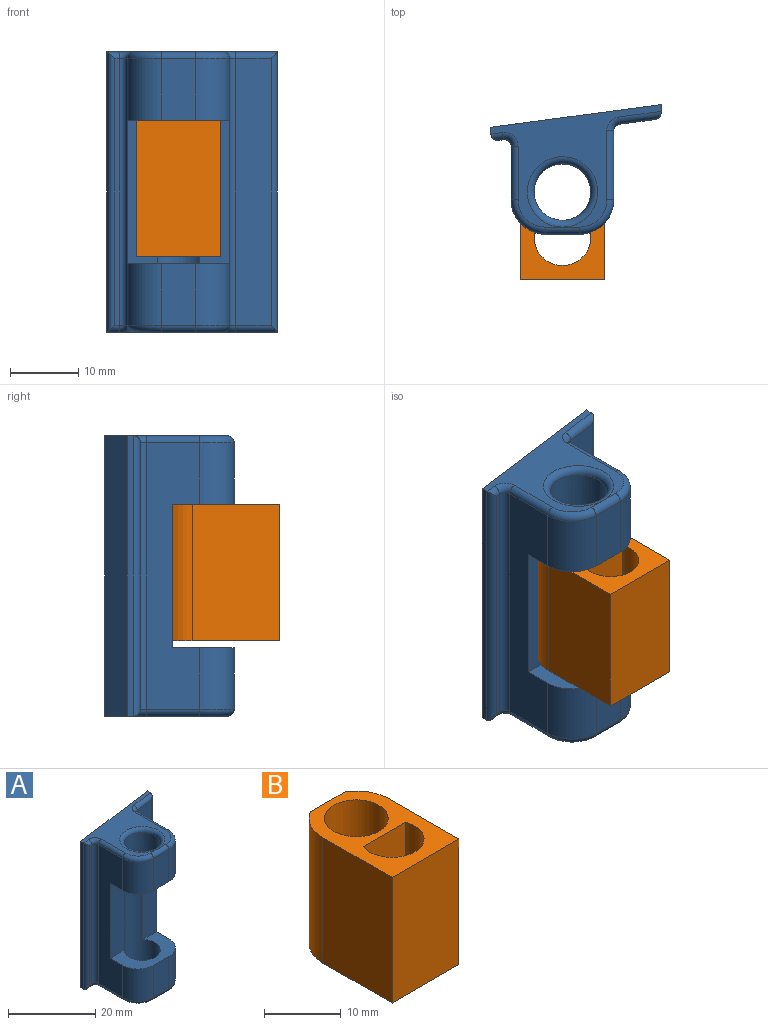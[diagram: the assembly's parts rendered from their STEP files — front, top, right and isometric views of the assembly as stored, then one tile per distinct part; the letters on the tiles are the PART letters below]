
ASSEMBLY  parts=2 mates=1
PART A: 44 faces, bbox 25x19.3x41 mm
  f0: plane 9x5mm, normal (0,-1,0), area 45mm2, adj f4,f5,f37,f42
  f1: plane 39x10.12mm, normal (1,0,0), area 310.9mm2, adj f4,f14,f19,f27,f33,f40,f42,f43
  f2: plane 39x7.86mm, normal (-1,0,0), area 222.5mm2, adj f5,f15,f22,f30,f34,f41,f42,f43
  f3: cylinder r=4.15mm len=39mm, axis (0,0,-1), area 611.2mm2, adj f38,f39,f40,f41,f42,f43
  f4: cylinder r=5mm len=9mm, axis (0,0,-1), area 70.7mm2, adj f0,f1,f35,f42
  f5: cylinder r=5mm len=9mm, axis (0,0,1), area 70.7mm2, adj f0,f2,f36,f42
  f6: plane 24.91x17.93mm, normal (0,0,-1), area 131.4mm2, adj f7,f9,f10,f25,f28,f29,f31,f32
  f7: plane 41x24.91mm, normal (-0.13,0.99,0), area 1030.4mm2, adj f6,f9,f10,f13
  f8: plane 39x5.2mm, normal (0.13,-0.99,0), area 204.7mm2, adj f20,f24,f27,f28
  f9: plane 41x1.12mm, normal (1,0,0), area 46.1mm2, adj f6,f7,f13,f20,f24,f28
  f10: plane 41x0.86mm, normal (-1,0,0), area 35.2mm2, adj f6,f7,f13,f25
  f11: plane 39x0.71mm, normal (0.13,-0.99,0), area 27.9mm2, adj f21,f25,f29,f30
  f12: plane 9x5mm, normal (0,-1,0), area 45mm2, adj f14,f15,f16,f43
  f13: plane 24.91x17.93mm, normal (0,0,1), area 131.4mm2, adj f7,f9,f10,f16,f17,f18,f19,f20
  f14: cylinder r=5mm len=9mm, axis (0,0,-1), area 70.7mm2, adj f1,f12,f17,f43
  f15: cylinder r=5mm len=9mm, axis (0,0,1), area 70.7mm2, adj f2,f12,f18,f43
  f16: cylinder r=1mm len=5mm, axis (1,0,0), area 7.9mm2, adj f12,f13,f17,f18
  f17: torus R=4mm, axis (0,0,-1), area 11.4mm2, adj f13,f14,f16,f19
  f18: torus R=4mm, axis (0,0,-1), area 11.4mm2, adj f13,f15,f16,f22
  f19: cylinder r=1mm len=10.12mm, axis (0,1,0), area 15.9mm2, adj f1,f13,f17,f23
  f20: cylinder r=1mm len=6.34mm, axis (-0.99,-0.13,0), area 9.2mm2, adj f8,f9,f13,f23,f24
  f21: cylinder r=1mm len=1.83mm, axis (-0.99,-0.13,0), area 2.1mm2, adj f11,f13,f25,f26
  f22: cylinder r=1mm len=7.86mm, axis (0,-1,0), area 12.3mm2, adj f2,f13,f18,f26
  f23: torus R=2mm, axis (0,0,-1), area 3.1mm2, adj f13,f19,f20,f27
  f24: cylinder r=1mm len=40.98mm, axis (0,0,1), area 57.8mm2, adj f8,f9,f20,f28
  f25: cylinder r=1mm len=41mm, axis (0,0,1), area 68.7mm2, adj f6,f10,f11,f13,f21,f29
  f26: torus R=2mm, axis (0,0,-1), area 3.6mm2, adj f13,f21,f22,f30
  f27: cylinder r=1mm len=39mm, axis (0,0,-1), area 56.1mm2, adj f1,f8,f23,f31
  f28: cylinder r=1mm len=6.34mm, axis (0.99,0.13,0), area 9.2mm2, adj f6,f8,f9,f24,f31
  f29: cylinder r=1mm len=1.83mm, axis (0.99,0.13,0), area 2.1mm2, adj f6,f11,f25,f32
  f30: cylinder r=1mm len=39mm, axis (0,0,-1), area 66.4mm2, adj f2,f11,f26,f32
  f31: torus R=2mm, axis (0,0,-1), area 3.1mm2, adj f6,f27,f28,f33
  f32: torus R=2mm, axis (0,0,-1), area 3.6mm2, adj f6,f29,f30,f34
  f33: cylinder r=1mm len=10.12mm, axis (0,-1,0), area 15.9mm2, adj f1,f6,f31,f35
  f34: cylinder r=1mm len=7.86mm, axis (0,1,0), area 12.3mm2, adj f2,f6,f32,f36
  f35: torus R=4mm, axis (0,0,-1), area 11.4mm2, adj f4,f6,f33,f37
  f36: torus R=4mm, axis (0,0,-1), area 11.4mm2, adj f5,f6,f34,f37
  f37: cylinder r=1mm len=5mm, axis (-1,0,0), area 7.9mm2, adj f0,f6,f35,f36
  f38: torus R=5.15mm, axis (0,0,-1), area 44.5mm2, adj f3,f13
  f39: torus R=5.15mm, axis (0,0,-1), area 44.5mm2, adj f3,f6
  f40: plane 21x4.48mm, normal (0,-1,0), area 94.2mm2, adj f1,f3,f42,f43
  f41: plane 21x4.48mm, normal (0,-1,0), area 94.2mm2, adj f2,f3,f42,f43
  f42: plane 15x9mm, normal (0,0,1), area 75.6mm2, adj f0,f1,f2,f3,f4,f5,f40,f41
  f43: plane 15x9mm, normal (0,0,-1), area 75.6mm2, adj f1,f2,f3,f12,f14,f15,f40,f41
PART B: 11 faces, bbox 12.3x18x20 mm
  f0: plane 20x12.75mm, normal (-1,0,0), area 255mm2, adj f1,f6,f9,f10
  f1: plane 20x12.3mm, normal (0,-1,0), area 246mm2, adj f0,f2,f9,f10
  f2: plane 20x12.75mm, normal (1,0,0), area 255mm2, adj f1,f3,f9,f10
  f3: cylinder r=6.15mm len=20mm, axis (0,0,-1), area 125.8mm2, adj f2,f4,f9,f10
  f4: plane 20x6.41mm, normal (0,1,0), area 128.1mm2, adj f3,f6,f9,f10
  f5: cylinder r=4.15mm len=20mm, axis (0,0,-1), area 320mm2, adj f7,f9,f10
  f6: cylinder r=6.15mm len=20mm, axis (0,0,-1), area 125.8mm2, adj f0,f4,f9,f10
  f7: plane 20x7.78mm, normal (0,-1,0), area 155.5mm2, adj f5,f9,f10
  f8: cylinder r=4.15mm len=20mm, axis (0,0,-1), area 521.5mm2, adj f9,f10
  f9: plane 18x12.3mm, normal (0,0,1), area 119.4mm2, adj f0,f1,f2,f3,f4,f5,f6,f7
  f10: plane 18x12.3mm, normal (0,0,-1), area 119.4mm2, adj f0,f1,f2,f3,f4,f5,f6,f7
PLACE A t=(-26.61,-10.51,-2.72)mm
PLACE B t=(-26.61,-26.11,-0.72)mm
MATE revolute B.f8 <-> A.f3  axis (0,0,-1) through (-26.61,-22.36,19.28)mm
